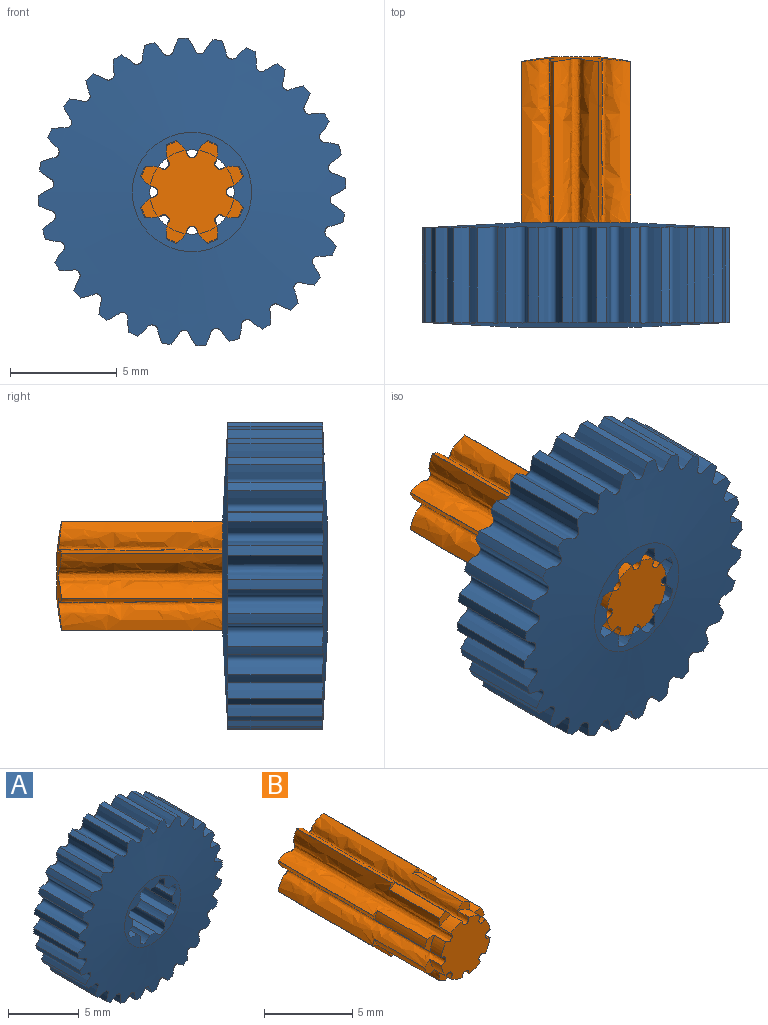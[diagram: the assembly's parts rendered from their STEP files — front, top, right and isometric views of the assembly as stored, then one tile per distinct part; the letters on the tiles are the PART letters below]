
ASSEMBLY  parts=2 mates=1
PART A: 76 faces, bbox 14.5x4.9x14.5 mm
  f0: cylinder r=1.98mm len=4.9mm, axis (0,1,0), area 2.9mm2, adj f23,f25,f26,f61
  f1: cylinder r=1.98mm len=4.9mm, axis (0,1,0), area 2.9mm2, adj f23,f26,f27,f61
  f2: cylinder r=1.98mm len=4.9mm, axis (0,1,0), area 2.9mm2, adj f23,f27,f28,f61
  f3: cylinder r=1.98mm len=4.9mm, axis (0,1,0), area 2.9mm2, adj f23,f28,f29,f61
  f4: cylinder r=1.98mm len=4.9mm, axis (0,1,0), area 2.9mm2, adj f23,f29,f30,f61
  f5: cylinder r=1.98mm len=4.9mm, axis (0,1,0), area 2.9mm2, adj f23,f30,f31,f61
  f6: cylinder r=1.98mm len=4.9mm, axis (0,1,0), area 2.9mm2, adj f23,f25,f32,f61
  f7: cylinder r=1.98mm len=4.9mm, axis (0,1,0), area 2.9mm2, adj f23,f31,f32,f61
  f8: cylinder r=7.22mm len=4.44mm, axis (0,1,0), area 2mm2, adj f24,f33,f59,f75
  f9: cylinder r=7.22mm len=4.44mm, axis (0,1,0), area 2mm2, adj f33,f34,f59,f75
  f10: cylinder r=7.22mm len=4.44mm, axis (0,1,0), area 2mm2, adj f34,f35,f59,f75
  f11: cylinder r=7.22mm len=4.44mm, axis (0,1,0), area 2mm2, adj f35,f36,f59,f75
  f12: cylinder r=7.22mm len=4.44mm, axis (0,1,0), area 2mm2, adj f36,f37,f59,f75
  f13: cylinder r=7.22mm len=4.44mm, axis (0,1,0), area 2mm2, adj f37,f38,f59,f75
  f14: cylinder r=7.22mm len=4.44mm, axis (0,1,0), area 2mm2, adj f38,f39,f59,f75
  f15: cylinder r=7.22mm len=4.44mm, axis (0,1,0), area 2mm2, adj f39,f40,f59,f75
  f16: cylinder r=7.22mm len=4.44mm, axis (0,1,0), area 2mm2, adj f40,f41,f59,f75
  f17: cylinder r=7.22mm len=4.44mm, axis (0,1,0), area 2mm2, adj f41,f42,f59,f75
  f18: cylinder r=7.22mm len=4.44mm, axis (0,1,0), area 2mm2, adj f42,f43,f59,f75
  f19: cylinder r=7.22mm len=4.44mm, axis (0,1,0), area 2mm2, adj f43,f44,f59,f75
  f20: cylinder r=7.22mm len=4.44mm, axis (0,1,0), area 2mm2, adj f44,f45,f59,f75
  f21: cylinder r=7.22mm len=4.44mm, axis (0,1,0), area 2mm2, adj f22,f45,f59,f75
  f22: bspline ~4.57x1.08mm, area 8.4mm2, adj f21,f46,f59,f75
  f23: plane 5.62x5.62mm, normal (0,-1,0), area 9mm2, adj f0,f1,f2,f3,f4,f5,f6,f7
  f24: bspline ~4.57x1.08mm, area 8.4mm2, adj f8,f59,f60,f75
  f25: bspline ~4.9x0.92mm, area 8.6mm2, adj f0,f6,f23,f61
  f26: bspline ~4.9x0.92mm, area 8.6mm2, adj f0,f1,f23,f61
  f27: bspline ~4.9x0.92mm, area 8.6mm2, adj f1,f2,f23,f61
  f28: bspline ~4.9x0.92mm, area 8.6mm2, adj f2,f3,f23,f61
  f29: bspline ~4.9x0.92mm, area 8.6mm2, adj f3,f4,f23,f61
  f30: bspline ~4.9x0.92mm, area 8.6mm2, adj f4,f5,f23,f61
  f31: bspline ~4.9x0.92mm, area 8.6mm2, adj f5,f7,f23,f61
  f32: bspline ~4.9x0.92mm, area 8.6mm2, adj f6,f7,f23,f61
  f33: bspline ~4.57x1.15mm, area 8.4mm2, adj f8,f9,f59,f75
  f34: bspline ~4.57x1.16mm, area 8.4mm2, adj f9,f10,f59,f75
  f35: bspline ~4.57x1.12mm, area 8.4mm2, adj f10,f11,f59,f75
  f36: bspline ~4.57x1.02mm, area 8.4mm2, adj f11,f12,f59,f75
  f37: bspline ~4.57x0.99mm, area 8.4mm2, adj f12,f13,f59,f75
  f38: bspline ~4.57x0.99mm, area 8.4mm2, adj f13,f14,f59,f75
  f39: bspline ~4.57x1.08mm, area 8.4mm2, adj f14,f15,f59,f75
  f40: bspline ~4.57x1.15mm, area 8.4mm2, adj f15,f16,f59,f75
  f41: bspline ~4.57x1.16mm, area 8.4mm2, adj f16,f17,f59,f75
  f42: bspline ~4.57x1.12mm, area 8.4mm2, adj f17,f18,f59,f75
  f43: bspline ~4.57x1.02mm, area 8.4mm2, adj f18,f19,f59,f75
  f44: bspline ~4.57x0.99mm, area 8.4mm2, adj f19,f20,f59,f75
  f45: bspline ~4.57x0.99mm, area 8.4mm2, adj f20,f21,f59,f75
  f46: cylinder r=7.22mm len=4.44mm, axis (0,1,0), area 2mm2, adj f22,f59,f62,f75
  f47: cylinder r=7.22mm len=4.44mm, axis (0,1,0), area 2mm2, adj f59,f62,f63,f75
  f48: cylinder r=7.22mm len=4.44mm, axis (0,1,0), area 2mm2, adj f59,f63,f64,f75
  f49: cylinder r=7.22mm len=4.44mm, axis (0,1,0), area 2mm2, adj f59,f64,f65,f75
  f50: cylinder r=7.22mm len=4.44mm, axis (0,1,0), area 2mm2, adj f59,f65,f66,f75
  f51: cylinder r=7.22mm len=4.44mm, axis (0,1,0), area 2mm2, adj f59,f66,f67,f75
  f52: cylinder r=7.22mm len=4.44mm, axis (0,1,0), area 2mm2, adj f59,f67,f68,f75
  f53: cylinder r=7.22mm len=4.44mm, axis (0,1,0), area 2mm2, adj f59,f68,f69,f75
  f54: cylinder r=7.22mm len=4.44mm, axis (0,1,0), area 2mm2, adj f59,f69,f70,f75
  f55: cylinder r=7.22mm len=4.44mm, axis (0,1,0), area 2mm2, adj f59,f70,f71,f75
  f56: cylinder r=7.22mm len=4.44mm, axis (0,1,0), area 2mm2, adj f59,f71,f72,f75
  f57: cylinder r=7.22mm len=4.44mm, axis (0,1,0), area 2mm2, adj f59,f72,f73,f75
  f58: cylinder r=7.22mm len=4.44mm, axis (0,1,0), area 2mm2, adj f59,f73,f74,f75
  f59: cone r=7.22mm half-angle=87deg, axis (0,1,0), area 125.2mm2, adj f8,f9,f10,f11,f12,f13,f14,f15
  f60: cylinder r=7.22mm len=4.44mm, axis (0,1,0), area 2mm2, adj f24,f59,f74,f75
  f61: plane 5.62x5.62mm, normal (0,1,0), area 9mm2, adj f0,f1,f2,f3,f4,f5,f6,f7
  f62: bspline ~4.57x1.15mm, area 8.4mm2, adj f46,f47,f59,f75
  f63: bspline ~4.57x1.16mm, area 8.4mm2, adj f47,f48,f59,f75
  f64: bspline ~4.57x1.12mm, area 8.4mm2, adj f48,f49,f59,f75
  f65: bspline ~4.57x1.02mm, area 8.4mm2, adj f49,f50,f59,f75
  f66: bspline ~4.57x0.99mm, area 8.4mm2, adj f50,f51,f59,f75
  f67: bspline ~4.57x0.99mm, area 8.4mm2, adj f51,f52,f59,f75
  f68: bspline ~4.57x1.08mm, area 8.4mm2, adj f52,f53,f59,f75
  f69: bspline ~4.57x1.15mm, area 8.4mm2, adj f53,f54,f59,f75
  f70: bspline ~4.57x1.16mm, area 8.4mm2, adj f54,f55,f59,f75
  f71: bspline ~4.57x1.12mm, area 8.4mm2, adj f55,f56,f59,f75
  f72: bspline ~4.57x1.02mm, area 8.4mm2, adj f56,f57,f59,f75
  f73: bspline ~4.57x0.99mm, area 8.4mm2, adj f57,f58,f59,f75
  f74: bspline ~4.57x0.99mm, area 8.4mm2, adj f58,f59,f60,f75
  f75: cone r=7.22mm half-angle=87deg, axis (0,-1,0), area 125.3mm2, adj f8,f9,f10,f11,f12,f13,f14,f15
PART B: 67 faces, bbox 5.6x12.7x5.6 mm
  f0: cylinder r=2.48mm len=4mm, axis (0,-1,0), area 2.2mm2, adj f4,f20,f21,f26
  f1: plane 2.12x0.01mm, normal (0.38,0,-0.92), area 0mm2, adj f2,f20,f21,f61
  f2: cylinder r=2.77mm len=4mm, axis (0,-1,0), area 0mm2, adj f1,f3,f20,f21
  f3: plane 1.45x0.01mm, normal (0.38,0,-0.92), area 0mm2, adj f2,f4,f20,f21
  f4: plane 0.52x0.4mm, normal (0,-1,0), area 0.1mm2, adj f0,f3,f20,f21
  f5: cylinder r=2.48mm len=4mm, axis (0,-1,0), area 2.2mm2, adj f9,f21,f22,f27
  f6: plane 2.12x0.01mm, normal (-0.38,0,-0.92), area 0mm2, adj f7,f21,f22,f61
  f7: cylinder r=2.77mm len=4mm, axis (0,-1,0), area 0mm2, adj f6,f8,f21,f22
  f8: plane 1.45x0.01mm, normal (-0.38,0,-0.92), area 0mm2, adj f7,f9,f21,f22
  f9: plane 0.52x0.4mm, normal (0,-1,0), area 0.1mm2, adj f5,f8,f21,f22
  f10: cylinder r=2.48mm len=4mm, axis (0,-1,0), area 2.2mm2, adj f11,f20,f23,f25
  f11: plane 0.52x0.4mm, normal (0,-1,0), area 0.1mm2, adj f10,f12,f20,f23
  f12: plane 1.45x0.01mm, normal (0.92,0,-0.38), area 0mm2, adj f11,f13,f20,f23
  f13: cylinder r=2.77mm len=4mm, axis (0,-1,0), area 0mm2, adj f12,f14,f20,f23
  f14: plane 2.12x0.01mm, normal (0.92,0,-0.38), area 0mm2, adj f13,f20,f23,f61
  f15: cylinder r=2.48mm len=4mm, axis (0,-1,0), area 2.2mm2, adj f19,f22,f24,f28
  f16: plane 2.12x0.01mm, normal (-0.92,0,-0.38), area 0mm2, adj f17,f22,f24,f61
  f17: cylinder r=2.77mm len=4mm, axis (0,-1,0), area 0mm2, adj f16,f18,f22,f24
  f18: plane 1.45x0.01mm, normal (-0.92,0,-0.38), area 0mm2, adj f17,f19,f22,f24
  f19: plane 0.52x0.4mm, normal (0,-1,0), area 0.1mm2, adj f15,f18,f22,f24
  f20: bspline ~12.69x1.5mm, area 32.2mm2, adj f0,f1,f2,f3,f4,f10,f11,f12
  f21: bspline ~12.69x2.12mm, area 32.2mm2, adj f0,f1,f2,f3,f4,f5,f6,f7
  f22: bspline ~12.69x1.5mm, area 32.2mm2, adj f5,f6,f7,f8,f9,f15,f16,f17
  f23: bspline ~12.69x2.12mm, area 32.5mm2, adj f10,f11,f12,f13,f14,f25,f29,f30
  f24: bspline ~12.69x2.12mm, area 32.2mm2, adj f15,f16,f17,f18,f19,f28,f35,f36
  f25: plane 0.95x0.8mm, normal (0,-1,0), area 0.4mm2, adj f10,f20,f23,f42
  f26: plane 0.95x0.8mm, normal (0,-1,0), area 0.4mm2, adj f0,f20,f21,f43
  f27: plane 0.95x0.8mm, normal (0,-1,0), area 0.4mm2, adj f5,f21,f22,f44
  f28: plane 0.95x0.8mm, normal (0,-1,0), area 0.4mm2, adj f15,f22,f24,f45
  f29: plane 0.95x0.8mm, normal (0,-1,0), area 0.4mm2, adj f23,f30,f41,f48
  f30: cylinder r=2.48mm len=4mm, axis (0,-1,0), area 2.2mm2, adj f23,f29,f31,f48
  f31: plane 0.52x0.4mm, normal (0,-1,0), area 0.1mm2, adj f23,f30,f32,f48
  f32: plane 1.45x0.01mm, normal (0.92,0,0.38), area 0mm2, adj f23,f31,f33,f48
  f33: cylinder r=2.77mm len=4mm, axis (0,-1,0), area 0mm2, adj f23,f32,f34,f48
  f34: plane 2.12x0.01mm, normal (0.92,0,0.38), area 0mm2, adj f23,f33,f48,f61
  f35: cylinder r=2.48mm len=4mm, axis (0,-1,0), area 2.2mm2, adj f24,f36,f40,f49
  f36: plane 0.95x0.8mm, normal (0,-1,0), area 0.4mm2, adj f24,f35,f46,f49
  f37: plane 2.12x0.01mm, normal (-0.92,0,0.38), area 0mm2, adj f24,f38,f49,f61
  f38: cylinder r=2.77mm len=4mm, axis (0,-1,0), area 0mm2, adj f24,f37,f39,f49
  f39: plane 1.45x0.01mm, normal (-0.92,0,0.38), area 0mm2, adj f24,f38,f40,f49
  f40: plane 0.52x0.4mm, normal (0,-1,0), area 0.1mm2, adj f24,f35,f39,f49
  f41: cylinder r=1.98mm len=0.91mm, axis (0,-1,0), area 0.9mm2, adj f23,f29,f48,f53
  f42: cylinder r=1.98mm len=0.91mm, axis (0,-1,0), area 0.9mm2, adj f20,f23,f25,f53
  f43: cylinder r=1.98mm len=0.91mm, axis (0,-1,0), area 0.9mm2, adj f20,f21,f26,f53
  f44: cylinder r=1.98mm len=0.91mm, axis (0,-1,0), area 0.9mm2, adj f21,f22,f27,f53
  f45: cylinder r=1.98mm len=0.91mm, axis (0,-1,0), area 0.9mm2, adj f22,f24,f28,f53
  f46: cylinder r=1.98mm len=0.91mm, axis (0,-1,0), area 0.9mm2, adj f24,f36,f49,f53
  f47: plane 2x2mm, normal (0,1,0), area 3.1mm2, adj f61
  f48: bspline ~12.69x1.5mm, area 32.2mm2, adj f29,f30,f31,f32,f33,f34,f41,f53
  f49: bspline ~12.69x1.5mm, area 32.2mm2, adj f35,f36,f37,f38,f39,f40,f46,f50
  f50: cylinder r=2.48mm len=4mm, axis (0,-1,0), area 2.2mm2, adj f49,f51,f65,f66
  f51: plane 0.95x0.8mm, normal (0,-1,0), area 0.4mm2, adj f49,f50,f52,f66
  f52: cylinder r=1.98mm len=0.91mm, axis (0,-1,0), area 0.9mm2, adj f49,f51,f53,f66
  f53: plane 3.91x3.91mm, normal (0,-1,0), area 11mm2, adj f20,f21,f22,f23,f24,f41,f42,f43
  f54: cylinder r=1.98mm len=0.91mm, axis (0,-1,0), area 0.9mm2, adj f48,f53,f55,f66
  f55: plane 0.95x0.8mm, normal (0,-1,0), area 0.4mm2, adj f48,f54,f56,f66
  f56: cylinder r=2.48mm len=4mm, axis (0,-1,0), area 2.2mm2, adj f48,f55,f57,f66
  f57: plane 0.52x0.4mm, normal (0,-1,0), area 0.1mm2, adj f48,f56,f58,f66
  f58: plane 1.45x0.01mm, normal (0.38,0,0.92), area 0mm2, adj f48,f57,f59,f66
  f59: cylinder r=2.77mm len=4mm, axis (0,-1,0), area 0mm2, adj f48,f58,f60,f66
  f60: plane 2.12x0.01mm, normal (0.38,0,0.92), area 0mm2, adj f48,f59,f61,f66
  f61: cone r=2.77mm half-angle=82.5deg, axis (0,-1,0), area 12mm2, adj f1,f6,f14,f16,f20,f21,f22,f23
  f62: plane 2.12x0.01mm, normal (-0.38,0,0.92), area 0mm2, adj f49,f61,f63,f66
  f63: cylinder r=2.77mm len=4mm, axis (0,-1,0), area 0mm2, adj f49,f62,f64,f66
  f64: plane 1.45x0.01mm, normal (-0.38,0,0.92), area 0mm2, adj f49,f63,f65,f66
  f65: plane 0.52x0.4mm, normal (0,-1,0), area 0.1mm2, adj f49,f50,f64,f66
  f66: bspline ~12.69x2.12mm, area 32.2mm2, adj f50,f51,f52,f53,f54,f55,f56,f57
PLACE A t=(-4.27,-5.16,-0.96)mm
PLACE B t=(-4.27,-5.16,-0.96)mm
MATE fastened B.f0 <-> A.f0  axis (0,-1,0) through (-4.27,-13.51,-0.96)mm
